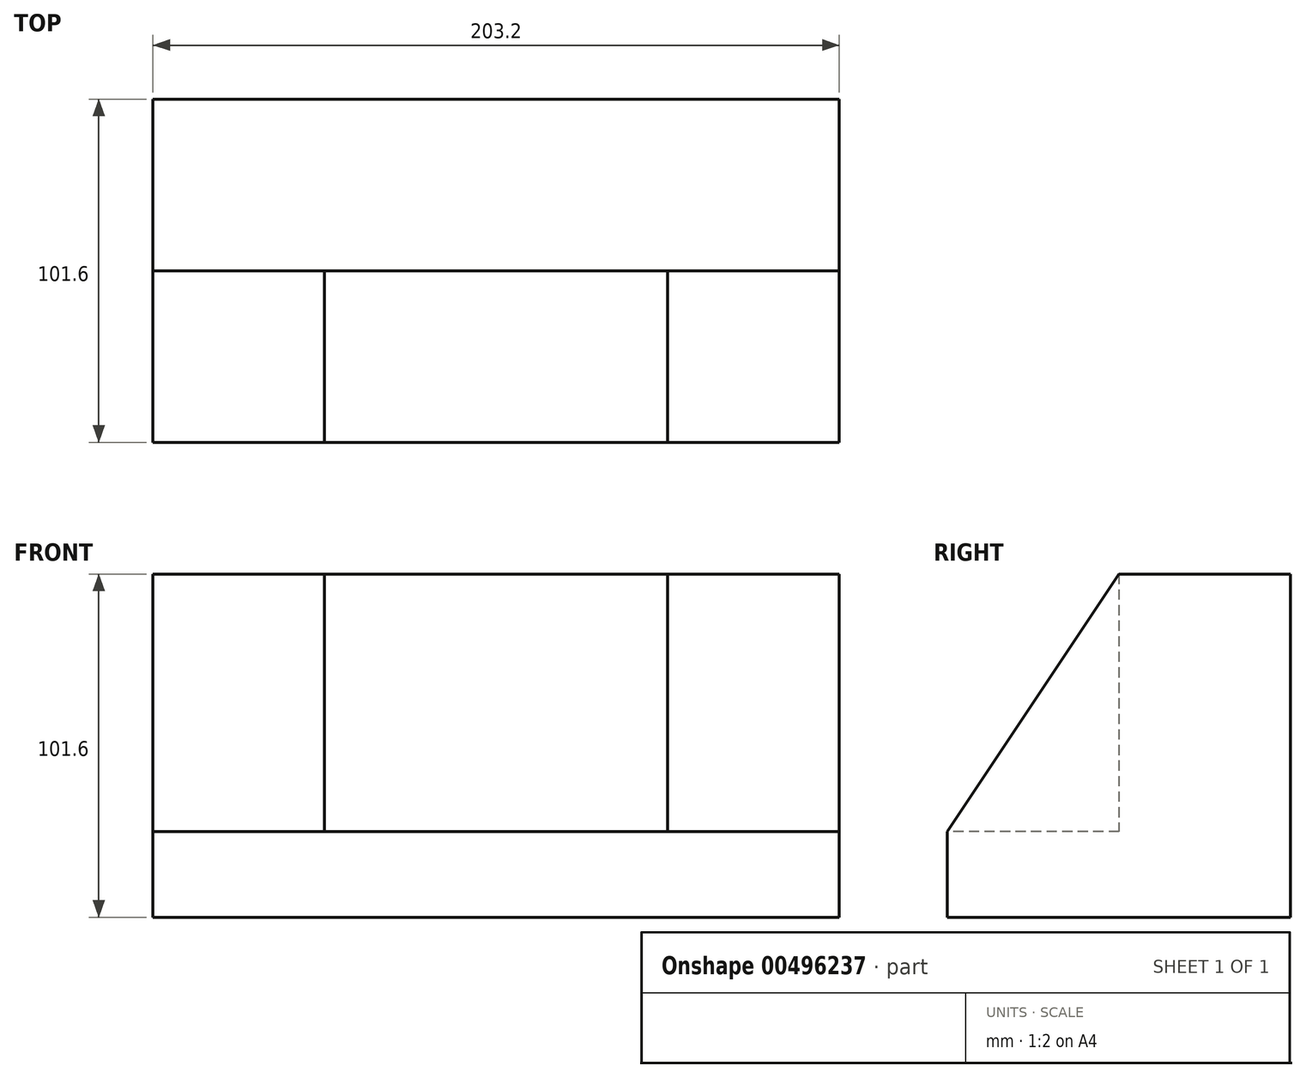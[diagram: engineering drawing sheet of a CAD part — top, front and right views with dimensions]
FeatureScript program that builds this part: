
annotation { "Feature Type Name" : "Feature", "Feature Type Description" : "" }
export const myFeature = defineFeature(function(context is Context, id is Id, definition is map)
    precondition{}
    {
        {
            var Q0;
            Q0=qCreatedBy(makeId("Front.planeOp"),FACE);
            var sketch = newSketch(context, id + "F0", { "sketchPlane" : qUnion([Q0])});
            skLineSegment(sketch, "E0.bottom", {"start": v(0, 0) * mm, "end": v(101.6, 0) * mm});
            skLineSegment(sketch, "E0.top", {"start": v(0, 101.6) * mm, "end": v(101.6, 101.6) * mm});
            skLineSegment(sketch, "E0.left", {"start": v(0, 0) * mm, "end": v(0, 101.6) * mm});
            skLineSegment(sketch, "E0.right", {"start": v(101.6, 0) * mm, "end": v(101.6, 101.6) * mm});
            skLineSegment(sketch, "E1", {"start": v(0, 0) * mm, "end": v(0, 25.4) * mm});
            skLineSegment(sketch, "E2", {"start": v(0, 25.4) * mm, "end": v(50.8, 25.4) * mm});
            skLineSegment(sketch, "E3", {"start": v(50.8, 25.4) * mm, "end": v(50.8, 101.6) * mm});
            skLineSegment(sketch, "E4", {"start": v(50.8, 101.6) * mm, "end": v(0, 25.4) * mm});
            skSolve(sketch);
        }
        {
            var Q0;
            Q0=makeQuery(id+"F0.imprint","IMPRINT",FACE,{"disambiguationData":[TD([[makeQuery(id+"F0.imprint","IMPRINT",EDGE,{"derivedFrom":sQuery(id+"F0.wireOp",EDGE,"E0.bottom")}),1.0]])]});
            var Q1;
            Q1=makeQuery(id+"F0.imprint","IMPRINT",FACE,{"disambiguationData":[TD([[makeQuery(id+"F0.imprint","IMPRINT",EDGE,{"derivedFrom":sQuery(id+"F0.wireOp",EDGE,"E2")}),1.0]])]});
            extrude(context, id + "F1", {"entities" : qUnion([Q0, Q1]), "depth" : 203.2 * mm});
        }
        {
            var Q0;
            Q0=makeQuery(id+"F1.opExtrude","CAP_FACE",FACE,{"disambiguationData":[OSD([sQuery(id+"F0.wireOp",EDGE,"E0.bottom"),sQuery(id+"F0.wireOp",EDGE,"E0.top"),sQuery(id+"F0.wireOp",EDGE,"E0.right"),sQuery(id+"F0.wireOp",EDGE,"E1"),sQuery(id+"F0.wireOp",EDGE,"E4")])],"isStart":true});
            var sketch = newSketch(context, id + "F2", { "sketchPlane" : qUnion([Q0])});
            skLineSegment(sketch, "E5", {"start": v(-50.8, 101.6) * mm, "end": v(-50.8, 25.4) * mm});
            skLineSegment(sketch, "E6", {"start": v(-50.8, 25.4) * mm, "end": v(0, 25.4) * mm});
            skSolve(sketch);
        }
        {
            var Q0;
            Q0=makeQuery(id+"F2.imprint","IMPRINT",FACE,{"disambiguationData":[TD([[makeQuery(id+"F2.imprint","IMPRINT",EDGE,{"derivedFrom":sQuery(id+"F2.wireOp",EDGE,"E5")}),1.0]])]});
            extrude(context, id + "F3", {"entities" : qUnion([Q0]), "operationType" : NewBodyOperationType.REMOVE, "oppositeDirection" : true, "depth" : 203.2 * mm});
        }
        {
            var Q0;
            Q0=makeQuery(id+"F1.opExtrude","CAP_FACE",FACE,{"disambiguationData":[OSD([sQuery(id+"F0.wireOp",EDGE,"E0.bottom"),sQuery(id+"F0.wireOp",EDGE,"E0.top"),sQuery(id+"F0.wireOp",EDGE,"E0.right"),sQuery(id+"F0.wireOp",EDGE,"E1"),sQuery(id+"F0.wireOp",EDGE,"E4")])],"isStart":true});
            var sketch = newSketch(context, id + "F4", { "sketchPlane" : qUnion([Q0])});
            skLineSegment(sketch, "E7", {"start": v(-50.8, 101.6) * mm, "end": v(0, 25.4) * mm});
            skLineSegment(sketch, "E8", {"start": v(0, 25.4) * mm, "end": v(-50.8, 25.4) * mm});
            skLineSegment(sketch, "E9", {"start": v(-50.8, 25.4) * mm, "end": v(-50.8, 101.6) * mm});
            skSolve(sketch);
        }
        {
            var Q0;
            Q0=makeQuery(id+"F4.imprint","IMPRINT",FACE,{"disambiguationData":[TD([[makeQuery(id+"F4.imprint","IMPRINT",EDGE,{"derivedFrom":sQuery(id+"F4.wireOp",EDGE,"E7")}),-1.0]])]});
            extrude(context, id + "F5", {"entities" : qUnion([Q0]), "operationType" : NewBodyOperationType.ADD, "oppositeDirection" : true, "depth" : 50.8 * mm});
        }
        {
            var Q0;
            Q0=makeQuery(id+"F1.opExtrude","CAP_FACE",FACE,{"disambiguationData":[OSD([sQuery(id+"F0.wireOp",EDGE,"E0.bottom"),sQuery(id+"F0.wireOp",EDGE,"E0.top"),sQuery(id+"F0.wireOp",EDGE,"E0.right"),sQuery(id+"F0.wireOp",EDGE,"E1"),sQuery(id+"F0.wireOp",EDGE,"E4")])],"isStart":false});
            var sketch = newSketch(context, id + "F6", { "sketchPlane" : qUnion([Q0])});
            skLineSegment(sketch, "E10", {"start": v(0, 25.4) * mm, "end": v(50.8, 101.6) * mm});
            skLineSegment(sketch, "E11", {"start": v(50.8, 101.6) * mm, "end": v(50.8, 25.4) * mm});
            skLineSegment(sketch, "E12", {"start": v(50.8, 25.4) * mm, "end": v(0, 25.4) * mm});
            skSolve(sketch);
        }
        {
            var Q0;
            Q0 = qSketchRegion(id + "F6", true);
            extrude(context, id + "F7", {"entities" : qUnion([Q0]), "operationType" : NewBodyOperationType.ADD, "oppositeDirection" : true, "depth" : 50.8 * mm});
        }
        {
            var Q0;
            Q0=makeQuery(id+"F1.opExtrude","SWEPT_BODY",BODY,{"disambiguationData":[OSD([sQuery(id+"F0.wireOp",EDGE,"E0.bottom"),sQuery(id+"F0.wireOp",EDGE,"E0.top"),sQuery(id+"F0.wireOp",EDGE,"E0.right"),sQuery(id+"F0.wireOp",EDGE,"E1"),sQuery(id+"F0.wireOp",EDGE,"E4")])]});
            var Q1;
            Q1=makeQuery(id+"F1.opExtrude","CAP_EDGE",EDGE,{"disambiguationData":[OSD([sQuery(id+"F0.wireOp",EDGE,"E0.right")])],"isStart":false});
            transform(context, id + "F8", {"entities" : qUnion([Q0]), "transformType" : TransformType.ROTATION, "transformAxis" : qUnion([Q1]), "angle" : 90 * degree, "makeCopy" : false});
        }
    });
